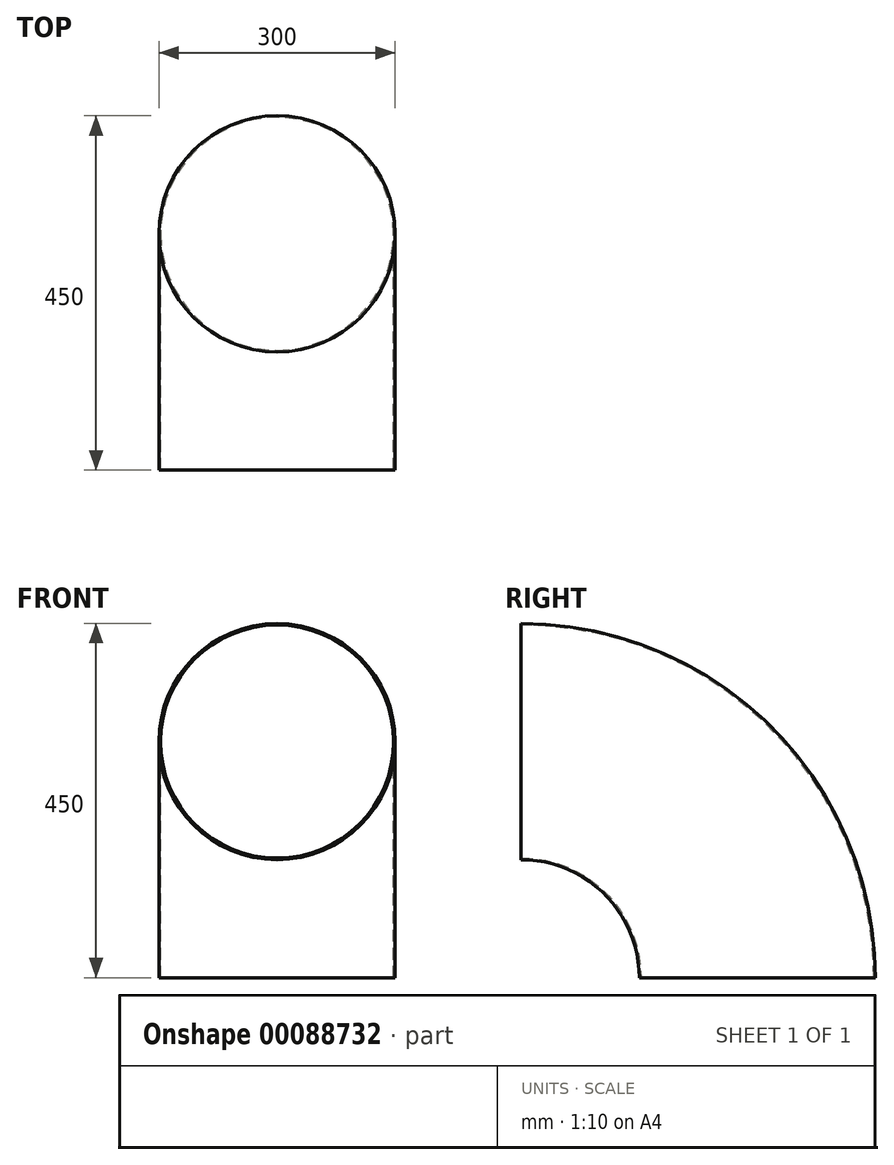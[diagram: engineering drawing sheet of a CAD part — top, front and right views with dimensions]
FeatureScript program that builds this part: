
annotation { "Feature Type Name" : "Feature", "Feature Type Description" : "" }
export const myFeature = defineFeature(function(context is Context, id is Id, definition is map)
    precondition{}
    {
        {
            var Q0;
            Q0=qCreatedBy(makeId("Front.planeOp"),FACE);
            var sketch = newSketch(context, id + "F0", { "sketchPlane" : qUnion([Q0])});
            skCircle(sketch, "E0", {"center": v(0, 0) * mm, "radius": 150 * mm});
            skCircle(sketch, "E1", {"center": v(0, 0) * mm, "radius": 148 * mm});
            skSolve(sketch);
        }
        {
            var Q0;
            Q0=qCreatedBy(makeId("Right.planeOp"),FACE);
            var sketch = newSketch(context, id + "F1", { "sketchPlane" : qUnion([Q0])});
            skLineSegment(sketch, "E2", {"start": v(0, 0) * mm, "end": v(0, 0) * mm});
            skLineSegment(sketch, "E3", {"start": v(300, -300) * mm, "end": v(300, -300) * mm});
            skPoint(sketch, "E4.visualSharp", {"position": v(300, 0) * mm});
            skArc(sketch, "E4.filletArc", {"start": v(300, -300) * mm, "mid": v(212.13, -87.87) * mm, "end": v(0, 0) * mm});
            skSolve(sketch);
        }
        {
            var Q0;
            Q0=makeQuery(id+"F0.imprint","IMPRINT",FACE,{"disambiguationData":[TD([[makeQuery(id+"F0.imprint","IMPRINT",EDGE,{"derivedFrom":sQuery(id+"F0.wireOp",EDGE,"E0")}),1.0]])]});
            var Q1;
            Q1=sQuery(id+"F1.wireOp",EDGE,"E2");
            var Q2;
            Q2=sQuery(id+"F1.wireOp",EDGE,"E4.filletArc");
            var Q3;
            Q3=sQuery(id+"F1.wireOp",EDGE,"E3");
            sweep(context, id + "F2", {"profiles" : qUnion([Q0]), "path" : qUnion([Q1, Q2, Q3])});
        }
    });
